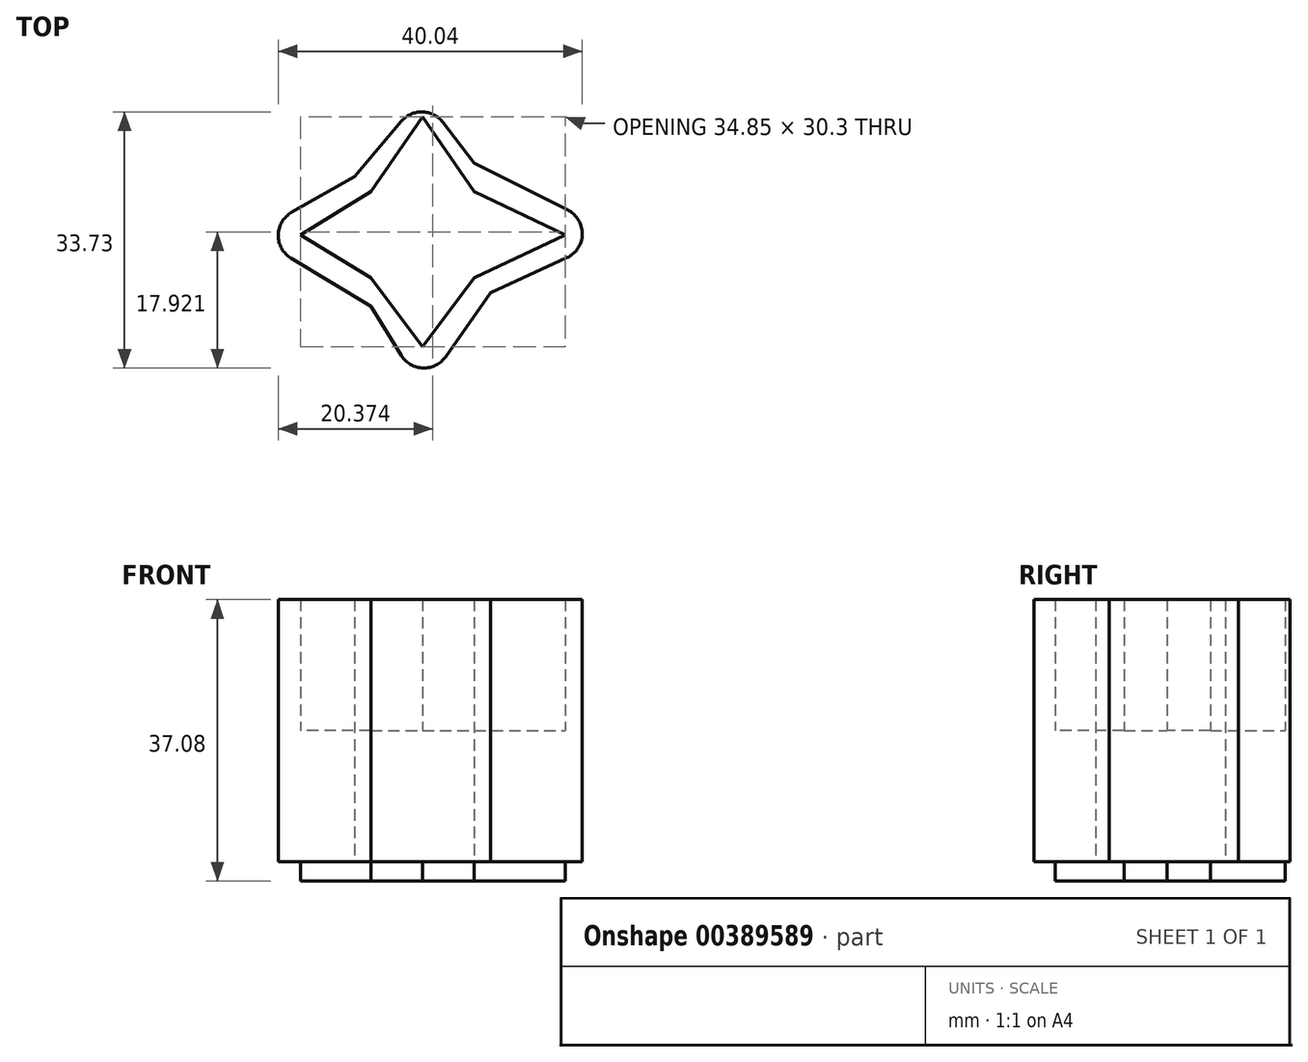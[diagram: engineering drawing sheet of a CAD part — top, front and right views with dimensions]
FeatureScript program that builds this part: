
annotation { "Feature Type Name" : "Feature", "Feature Type Description" : "" }
export const myFeature = defineFeature(function(context is Context, id is Id, definition is map)
    precondition{}
    {
        {
            var Q0;
            Q0=qCreatedBy(makeId("Top.planeOp"),FACE);
            var sketch = newSketch(context, id + "F0", { "sketchPlane" : qUnion([Q0])});
            skPoint(sketch, "E0.middle", {"position": v(0, 0) * mm});
            skLineSegment(sketch, "E1", {"start": v(-8.94, 7.64) * mm, "end": v(0, 18.25) * mm});
            skLineSegment(sketch, "E2", {"start": v(0, 18.25) * mm, "end": v(6.82, 9.41) * mm});
            skLineSegment(sketch, "E3", {"start": v(-8.94, 7.64) * mm, "end": v(-22.42, 0) * mm});
            skLineSegment(sketch, "E4", {"start": v(-22.42, 0) * mm, "end": v(-6.82, -9.41) * mm});
            skLineSegment(sketch, "E5", {"start": v(6.82, 9.41) * mm, "end": v(25.6, 0) * mm});
            skLineSegment(sketch, "E6", {"start": v(25.6, 0) * mm, "end": v(8.94, -7.64) * mm});
            skLineSegment(sketch, "E7", {"start": v(-6.82, -9.41) * mm, "end": v(0, -20.39) * mm});
            skLineSegment(sketch, "E8", {"start": v(8.94, -7.64) * mm, "end": v(0, -20.39) * mm});
            skLineSegment(sketch, "E9", {"start": v(-6.82, 5.69) * mm, "end": v(0, 15.52) * mm});
            skLineSegment(sketch, "E10", {"start": v(0, 15.52) * mm, "end": v(6.82, 5.69) * mm});
            skLineSegment(sketch, "E11", {"start": v(6.82, 5.69) * mm, "end": v(18.79, 0) * mm});
            skLineSegment(sketch, "E12", {"start": v(6.82, -5.69) * mm, "end": v(18.79, 0) * mm});
            skLineSegment(sketch, "E13", {"start": v(-6.82, 5.69) * mm, "end": v(-16.06, 0) * mm});
            skLineSegment(sketch, "E14", {"start": v(-16.06, 0) * mm, "end": v(-6.82, -5.69) * mm});
            skLineSegment(sketch, "E15", {"start": v(-6.82, -5.69) * mm, "end": v(0, -14.78) * mm});
            skLineSegment(sketch, "E16", {"start": v(6.82, -5.69) * mm, "end": v(0, -14.78) * mm});
            skSolve(sketch);
        }
        {
            var Q0;
            Q0 = qSketchRegion(id + "F0", true);
            extrude(context, id + "F1", {"entities" : qUnion([Q0]), "endBound" : BoundingType.SYMMETRIC, "depth" : 34.54 * mm});
        }
        {
            var Q0;
            Q0=makeQuery(id+"F0.imprint","IMPRINT",FACE,{"disambiguationData":[TD([[makeQuery(id+"F0.imprint","IMPRINT",EDGE,{"derivedFrom":sQuery(id+"F0.wireOp",EDGE,"E9")}),-1.0]])]});
            extrude(context, id + "F2", {"entities" : qUnion([Q0]), "operationType" : NewBodyOperationType.ADD, "oppositeDirection" : true, "depth" : 19.8 * mm});
        }
        {
            var Q0;
            Q0=makeQuery(id+"F1.opExtrude","SWEPT_EDGE",EDGE,{"disambiguationData":[OSD([sQuery(id+"F0.wireOp",EDGE,"E7"),sQuery(id+"F0.wireOp",EDGE,"E8")])]});
            var Q1;
            Q1=makeQuery(id+"F1.opExtrude","SWEPT_EDGE",EDGE,{"disambiguationData":[OSD([sQuery(id+"F0.wireOp",EDGE,"E3"),sQuery(id+"F0.wireOp",EDGE,"E4")])]});
            var Q2;
            Q2=makeQuery(id+"F1.opExtrude","SWEPT_EDGE",EDGE,{"disambiguationData":[OSD([sQuery(id+"F0.wireOp",EDGE,"E1"),sQuery(id+"F0.wireOp",EDGE,"E2")])]});
            var Q3;
            Q3=makeQuery(id+"F1.opExtrude","SWEPT_EDGE",EDGE,{"disambiguationData":[OSD([sQuery(id+"F0.wireOp",EDGE,"E5"),sQuery(id+"F0.wireOp",EDGE,"E6")])]});
            fillet(context, id + "F3", {"entities" : qUnion([Q0, Q1, Q2, Q3]), "radius" : 3.48 * mm, "tangentPropagation" : true, "allowEdgeOverflow" : false});
        }
    });
